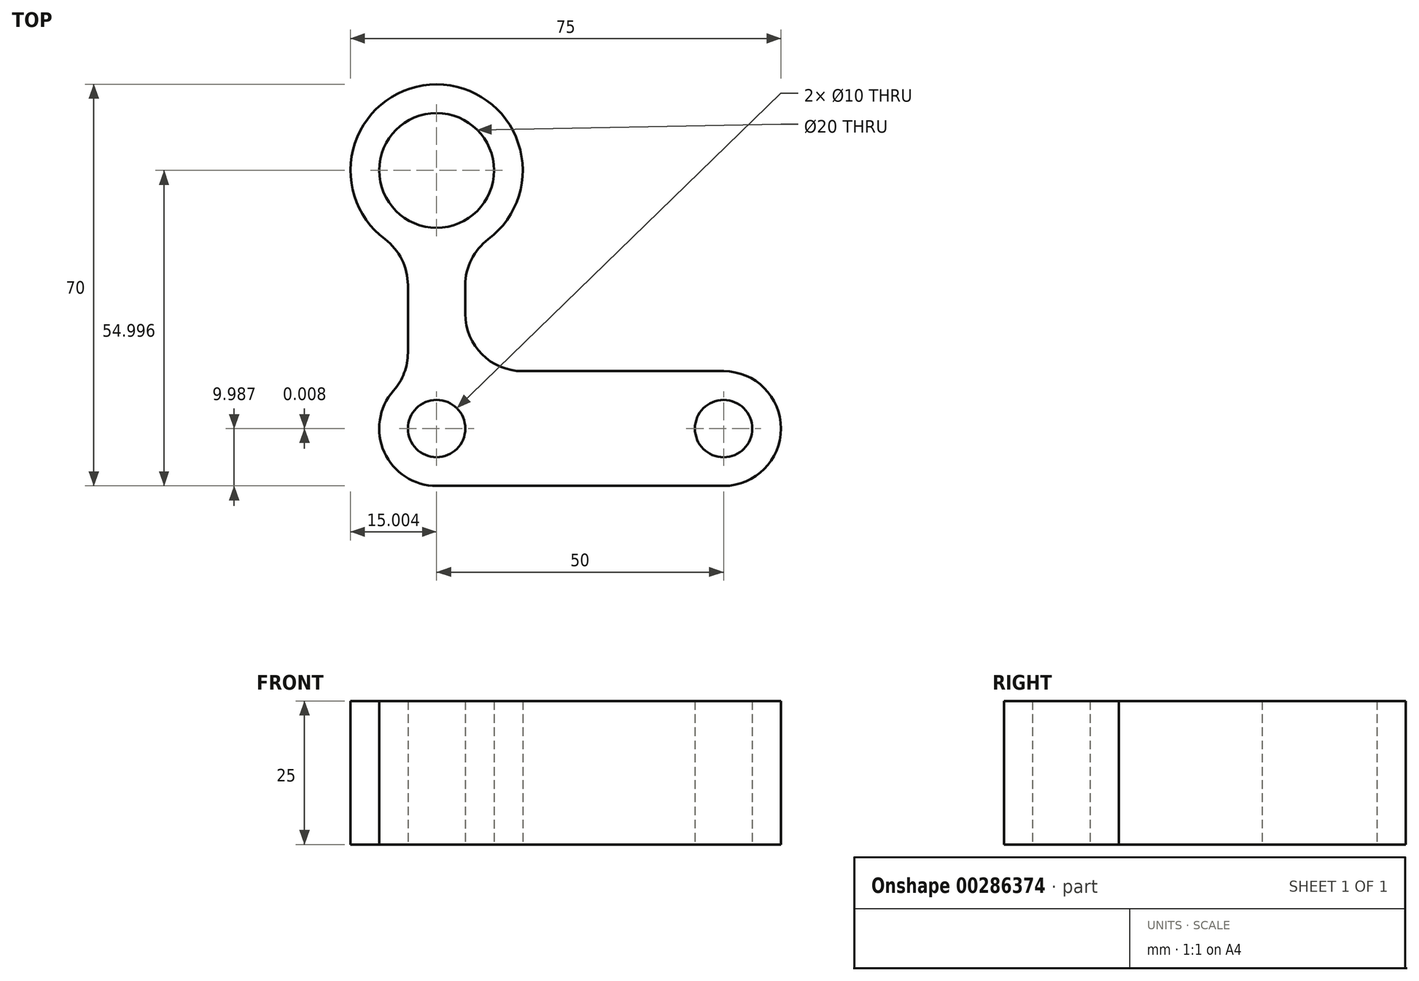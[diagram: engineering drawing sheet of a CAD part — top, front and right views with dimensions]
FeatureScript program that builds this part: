
annotation { "Feature Type Name" : "Feature", "Feature Type Description" : "" }
export const myFeature = defineFeature(function(context is Context, id is Id, definition is map)
    precondition{}
    {
        {
            var Q0;
            Q0=qCreatedBy(makeId("Top.planeOp"),FACE);
            var sketch = newSketch(context, id + "F0", { "sketchPlane" : qUnion([Q0])});
            skLineSegment(sketch, "E0", {"start": v(-29.08, -54.38) * mm, "end": v(20.92, -54.38) * mm});
            skLineSegment(sketch, "E1", {"start": v(30.92, -44.38) * mm, "end": v(30.92, -44.38) * mm});
            skCircle(sketch, "E2", {"center": v(20.92, -44.4) * mm, "radius": 5 * mm});
            skPoint(sketch, "E3.visualSharp", {"position": v(30.92, -54.38) * mm});
            skArc(sketch, "E3.filletArc", {"start": v(20.92, -54.38) * mm, "mid": v(28, -51.46) * mm, "end": v(30.92, -44.38) * mm});
            skLineSegment(sketch, "E4", {"start": v(7.76, -34.38) * mm, "end": v(20.92, -34.38) * mm});
            skPoint(sketch, "E5.orphan", {"position": v(30.92, 15.62) * mm});
            skPoint(sketch, "E6.visualSharp", {"position": v(30.92, -34.38) * mm});
            skArc(sketch, "E6.filletArc", {"start": v(30.92, -44.38) * mm, "mid": v(28, -37.31) * mm, "end": v(20.92, -34.38) * mm});
            skLineSegment(sketch, "E7", {"start": v(-39.08, -44.38) * mm, "end": v(-39.08, -44.38) * mm});
            skPoint(sketch, "E8.visualSharp", {"position": v(-39.08, -54.38) * mm});
            skArc(sketch, "E8.filletArc", {"start": v(-39.08, -44.38) * mm, "mid": v(-36.15, -51.46) * mm, "end": v(-29.08, -54.38) * mm});
            skCircle(sketch, "E9", {"center": v(-29.08, -44.38) * mm, "radius": 5 * mm});
            skPoint(sketch, "E10.visualSharp", {"position": v(-39.08, -34.38) * mm});
            skArc(sketch, "E10.filletArc", {"start": v(-36.58, -37.77) * mm, "mid": v(-38.43, -40.85) * mm, "end": v(-39.08, -44.38) * mm});
            skCircle(sketch, "E11", {"center": v(-29.08, 0.62) * mm, "radius": 10 * mm});
            skLineSegment(sketch, "E12", {"start": v(30.92, 15.62) * mm, "end": v(-61.46, 15.62) * mm});
            skArc(sketch, "E13", {"start": v(-20.08, -11.38) * mm, "mid": v(-29.08, 15.62) * mm, "end": v(-38.08, -11.38) * mm});
            skLineSegment(sketch, "E14", {"start": v(-29.08, -45.09) * mm, "end": v(-29.08, -44.38) * mm});
            skLineSegment(sketch, "E15", {"start": v(-24.08, -22.92) * mm, "end": v(-24.08, -19.38) * mm});
            skLineSegment(sketch, "E16", {"start": v(-34.08, -22.92) * mm, "end": v(-34.08, -19.38) * mm});
            skLineSegment(sketch, "E17", {"start": v(-34.08, -19.38) * mm, "end": v(-34.08, -31.16) * mm});
            skLineSegment(sketch, "E18", {"start": v(7.76, -34.38) * mm, "end": v(-14.08, -34.38) * mm});
            skLineSegment(sketch, "E19", {"start": v(-24.08, -24.38) * mm, "end": v(-24.08, -22.92) * mm});
            skPoint(sketch, "E20.visualSharp", {"position": v(-24.08, -34.38) * mm});
            skArc(sketch, "E20.filletArc", {"start": v(-24.08, -24.38) * mm, "mid": v(-21.15, -31.46) * mm, "end": v(-14.08, -34.38) * mm});
            skLineSegment(sketch, "E21.trimOffspring", {"start": v(-29.08, 10.62) * mm, "end": v(-29.08, 26.34) * mm});
            skPoint(sketch, "E22.visualSharp", {"position": v(-24.08, -13.53) * mm});
            skArc(sketch, "E22.filletArc", {"start": v(-20.08, -11.38) * mm, "mid": v(-23.02, -14.91) * mm, "end": v(-24.08, -19.38) * mm});
            skPoint(sketch, "E23.visualSharp", {"position": v(-34.08, -13.53) * mm});
            skArc(sketch, "E23.filletArc", {"start": v(-34.08, -19.38) * mm, "mid": v(-35.13, -14.91) * mm, "end": v(-38.08, -11.38) * mm});
            skPoint(sketch, "E24.visualSharp", {"position": v(-34.08, -35.72) * mm});
            skArc(sketch, "E24.filletArc", {"start": v(-36.58, -37.77) * mm, "mid": v(-34.72, -34.7) * mm, "end": v(-34.08, -31.16) * mm});
            skSolve(sketch);
        }
        {
            var Q0;
            Q0=makeQuery(id+"F0.imprint","IMPRINT",FACE,{"disambiguationData":[TD([[makeQuery(id+"F0.imprint","IMPRINT",EDGE,{"derivedFrom":sQuery(id+"F0.wireOp",EDGE,"E0")}),1.0]])]});
            extrude(context, id + "F1", {"entities" : qUnion([Q0]), "depth" : 25 * mm});
        }
    });
